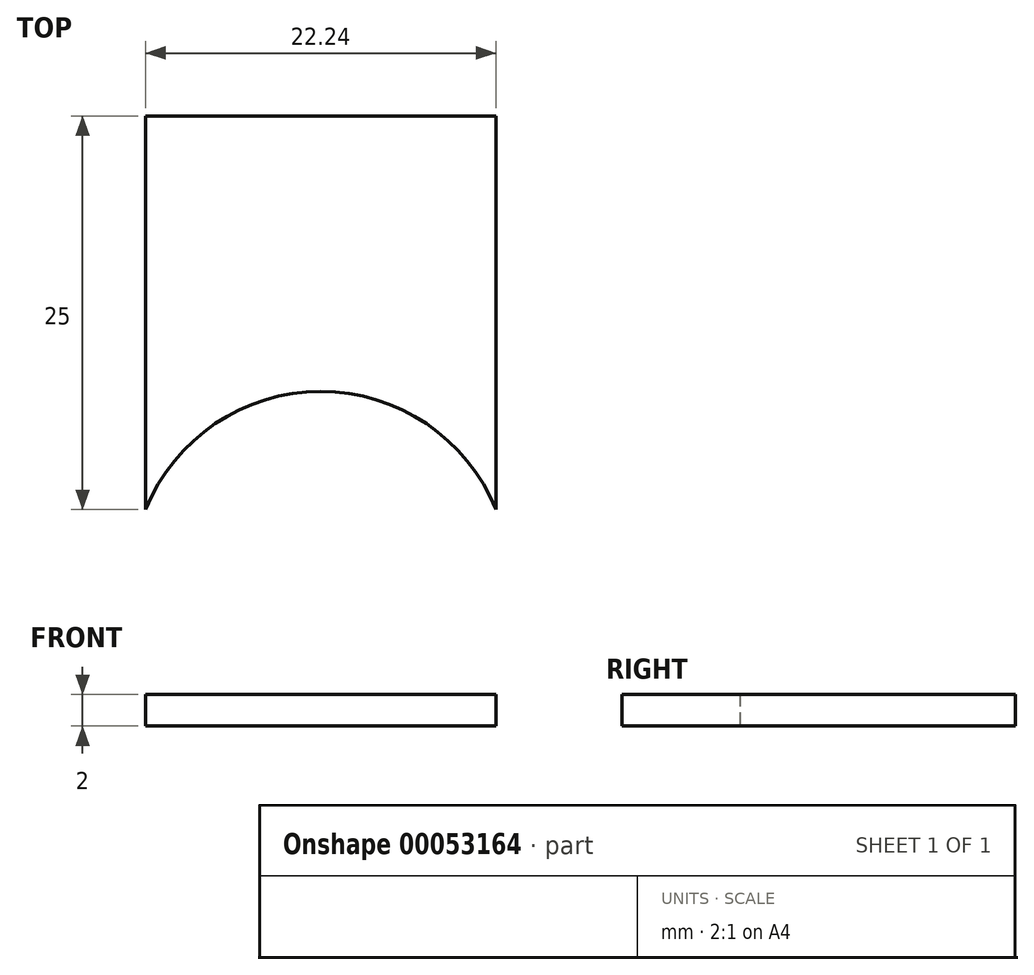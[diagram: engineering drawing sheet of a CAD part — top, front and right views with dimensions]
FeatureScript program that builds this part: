
annotation { "Feature Type Name" : "Feature", "Feature Type Description" : "" }
export const myFeature = defineFeature(function(context is Context, id is Id, definition is map)
    precondition{}
    {
        {
            var Q0;
            Q0=qCreatedBy(makeId("Top.planeOp"),FACE);
            var sketch = newSketch(context, id + "F0", { "sketchPlane" : qUnion([Q0])});
            skLineSegment(sketch, "E0.rect.bottom", {"start": v(-11.12, 25) * mm, "end": v(11.13, 25) * mm});
            skLineSegment(sketch, "E0.rect.left", {"start": v(-11.12, 25) * mm, "end": v(-11.12, 0) * mm});
            skLineSegment(sketch, "E0.rect.right", {"start": v(11.13, 25) * mm, "end": v(11.13, 0) * mm});
            skPoint(sketch, "E0.rect.middle", {"position": v(0, 0) * mm});
            skArc(sketch, "E1", {"start": v(11.13, 0) * mm, "mid": v(0, 7.5) * mm, "end": v(-11.12, 0) * mm});
            skPoint(sketch, "E0.rect.top.start.orphan", {"position": v(-11.12, -25) * mm});
            skPoint(sketch, "E2.orphan", {"position": v(11.13, -25) * mm});
            skLineSegment(sketch, "E3.bottom", {"start": v(-11.12, -25) * mm, "end": v(11.13, -25) * mm, "construction": true});
            skLineSegment(sketch, "E3.top", {"start": v(-11.12, 25) * mm, "end": v(11.13, 25) * mm, "construction": true});
            skLineSegment(sketch, "E3.left", {"start": v(-11.12, -25) * mm, "end": v(-11.12, 25) * mm, "construction": true});
            skLineSegment(sketch, "E3.right", {"start": v(11.13, -25) * mm, "end": v(11.13, 25) * mm, "construction": true});
            skSolve(sketch);
        }
        {
            var Q0;
            Q0=makeQuery(id+"F0.imprint","IMPRINT",FACE,{"disambiguationData":[TD([[makeQuery(id+"F0.imprint","IMPRINT",EDGE,{"derivedFrom":sQuery(id+"F0.wireOp",EDGE,"E0.rect.bottom")}),-1.0]])]});
            extrude(context, id + "F1", {"entities" : qUnion([Q0]), "depth" : 2 * mm});
        }
    });
